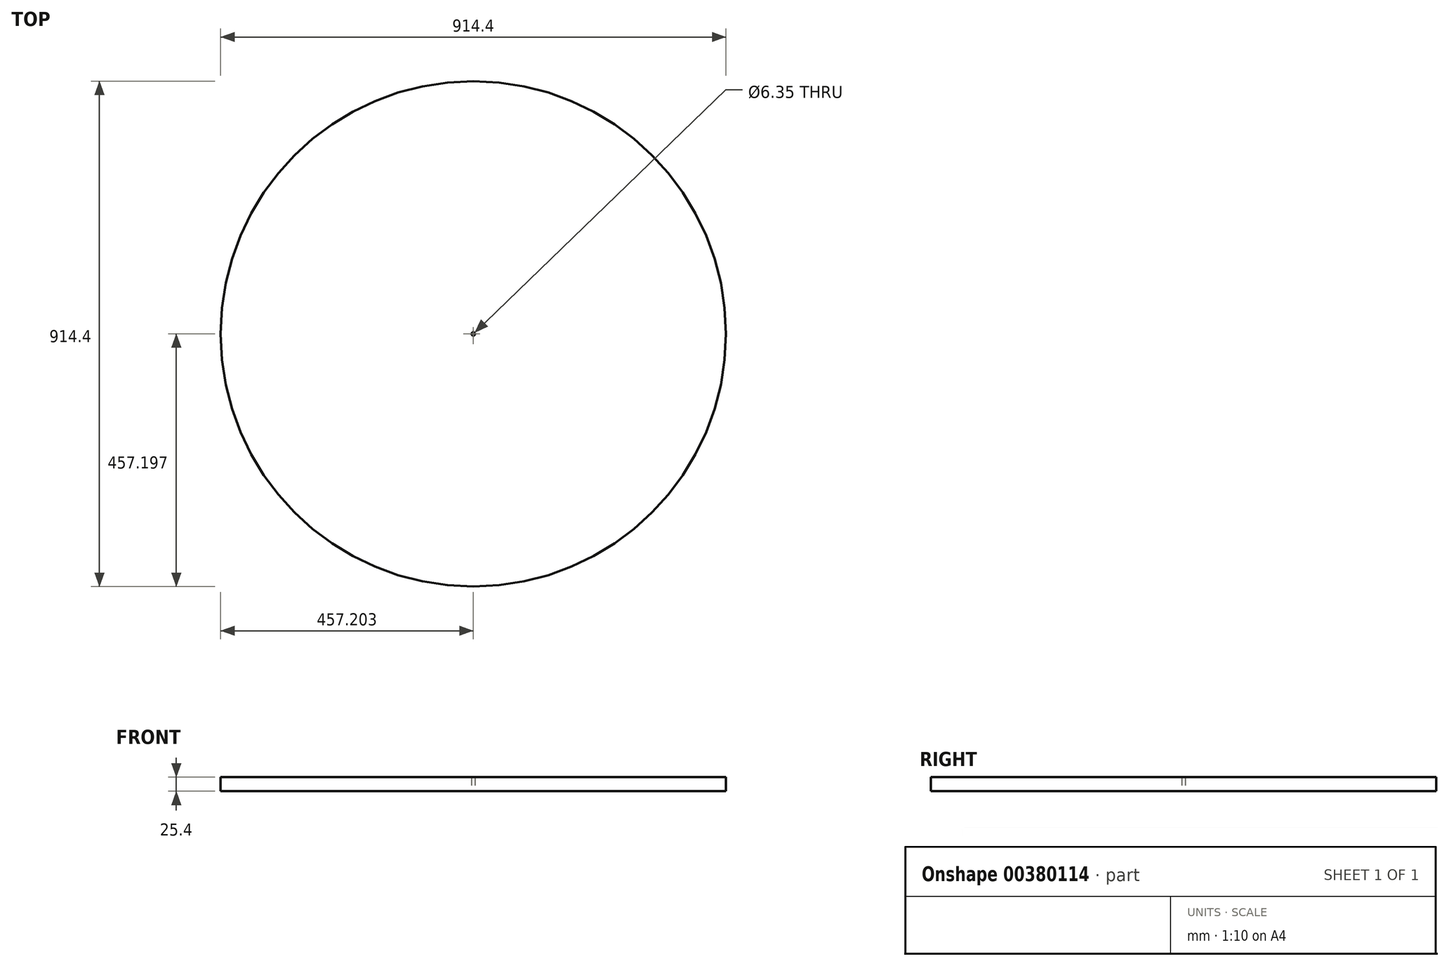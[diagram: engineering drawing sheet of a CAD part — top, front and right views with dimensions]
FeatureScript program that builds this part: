
annotation { "Feature Type Name" : "Feature", "Feature Type Description" : "" }
export const myFeature = defineFeature(function(context is Context, id is Id, definition is map)
    precondition{}
    {
        {
            var Q0;
            Q0=qCreatedBy(makeId("Top.planeOp"),FACE);
            var sketch = newSketch(context, id + "F0", { "sketchPlane" : qUnion([Q0])});
            skCircle(sketch, "E0", {"center": v(-8.17, 11.36) * mm, "radius": 457.2 * mm});
            skCircle(sketch, "E1", {"center": v(-8.17, 11.36) * mm, "radius": 3.18 * mm});
            skSolve(sketch);
        }
        {
            var Q0;
            Q0=qSketchRegion(id+"F0",true);
            extrude(context, id + "F1", {"entities" : qUnion([Q0]), "depth" : 25.4 * mm});
        }
    });
